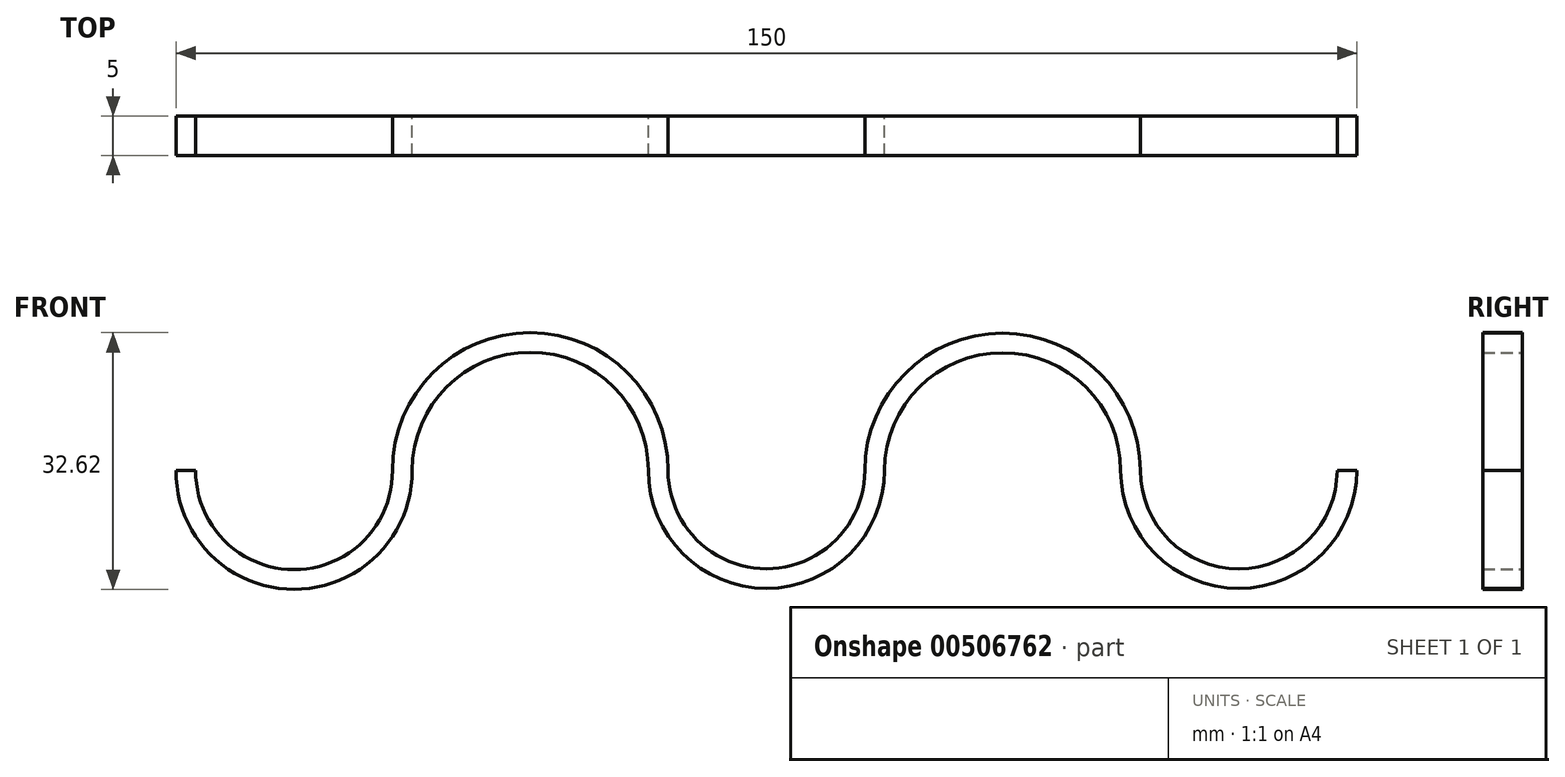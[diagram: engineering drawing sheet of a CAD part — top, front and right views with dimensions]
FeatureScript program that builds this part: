
annotation { "Feature Type Name" : "Feature", "Feature Type Description" : "" }
export const myFeature = defineFeature(function(context is Context, id is Id, definition is map)
    precondition{}
    {
        {
            var Q0;
            Q0=qCreatedBy(makeId("Front.planeOp"),FACE);
            var sketch = newSketch(context, id + "F0", { "sketchPlane" : qUnion([Q0])});
            skArc(sketch, "E0", {"start": v(-10.8, 0) * mm, "mid": v(-25.8, 15) * mm, "end": v(-40.8, 0) * mm});
            skArc(sketch, "E1", {"start": v(-10.8, 0) * mm, "mid": v(4.2, -15) * mm, "end": v(19.2, 0) * mm});
            skArc(sketch, "E2", {"start": v(49.2, 0) * mm, "mid": v(34.2, 14.94) * mm, "end": v(19.2, 0) * mm});
            skArc(sketch, "E3", {"start": v(-70.8, 0) * mm, "mid": v(-55.8, -15.12) * mm, "end": v(-40.8, 0) * mm});
            skArc(sketch, "E4", {"start": v(49.2, 0) * mm, "mid": v(50.46, -0.05) * mm, "end": v(51.7, 0) * mm});
            skLineSegment(sketch, "E5", {"start": v(-70.8, 0) * mm, "end": v(-68.3, 0) * mm});
            skLineSegment(sketch, "E6", {"start": v(-40.8, 0) * mm, "end": v(-43.3, 0) * mm});
            skLineSegment(sketch, "E7", {"start": v(-10.8, 0) * mm, "end": v(-8.3, 0) * mm});
            skLineSegment(sketch, "E8", {"start": v(51.7, 0) * mm, "end": v(49.2, 0) * mm});
            skArc(sketch, "E9", {"start": v(49.2, 0) * mm, "mid": v(64.2, -15) * mm, "end": v(79.2, 0) * mm});
            skLineSegment(sketch, "E10", {"start": v(79.2, 0) * mm, "end": v(76.7, 0) * mm});
            skLineSegment(sketch, "E11", {"start": v(19.2, 0) * mm, "end": v(16.7, 0) * mm});
            skArc(sketch, "E12", {"start": v(-68.3, 0) * mm, "mid": v(-55.8, -12.61) * mm, "end": v(-43.3, 0) * mm});
            skArc(sketch, "E13", {"start": v(-8.3, 0) * mm, "mid": v(-25.8, 17.5) * mm, "end": v(-43.3, 0) * mm});
            skArc(sketch, "E14", {"start": v(-8.3, 0) * mm, "mid": v(4.2, -12.5) * mm, "end": v(16.7, 0) * mm});
            skArc(sketch, "E15", {"start": v(51.7, 0) * mm, "mid": v(34.2, 17.43) * mm, "end": v(16.7, 0) * mm});
            skArc(sketch, "E16", {"start": v(51.7, 0) * mm, "mid": v(64.2, -12.5) * mm, "end": v(76.7, 0) * mm});
            skSolve(sketch);
        }
        {
            var Q0;
            Q0 = qSketchRegion(id + "F0", true);
            extrude(context, id + "F1", {"entities" : qUnion([Q0]), "depth" : 5 * mm});
        }
    });
